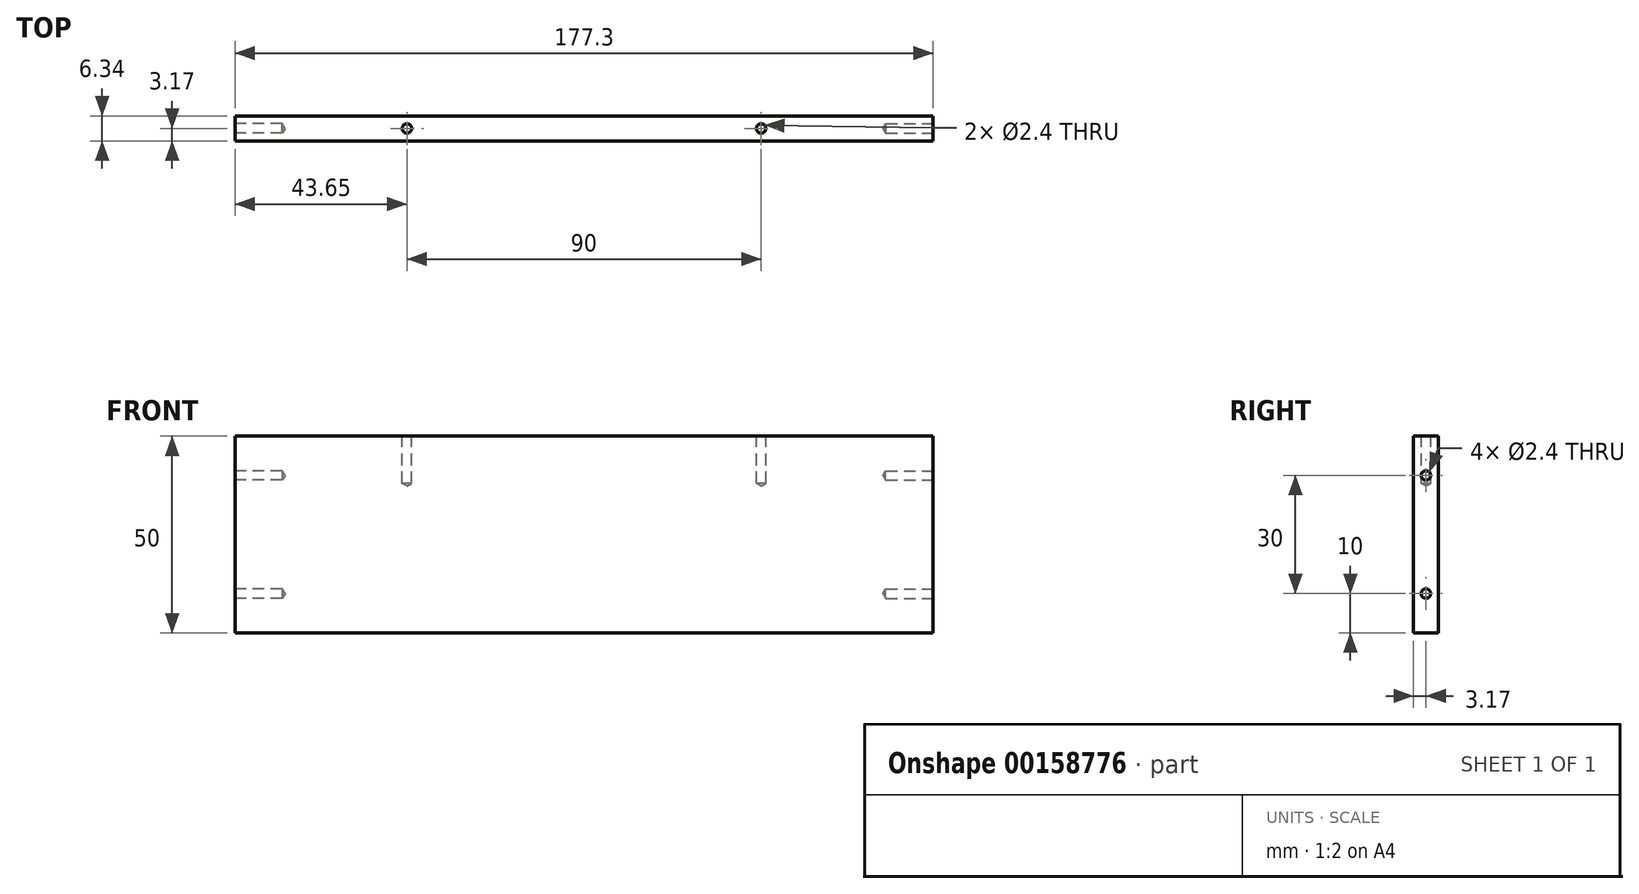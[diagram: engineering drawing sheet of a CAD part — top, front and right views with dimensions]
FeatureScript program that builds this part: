
annotation { "Feature Type Name" : "Feature", "Feature Type Description" : "" }
export const myFeature = defineFeature(function(context is Context, id is Id, definition is map)
    precondition{}
    {
        {
            var Q0;
            Q0=qCreatedBy(makeId("Front.planeOp"),FACE);
            var sketch = newSketch(context, id + "F0", { "sketchPlane" : qUnion([Q0])});
            skLineSegment(sketch, "E0.bottom", {"start": v(88.65, -25) * mm, "end": v(-88.65, -25) * mm});
            skLineSegment(sketch, "E0.top", {"start": v(88.65, 25) * mm, "end": v(-88.65, 25) * mm});
            skLineSegment(sketch, "E0.left", {"start": v(88.65, -25) * mm, "end": v(88.65, 25) * mm});
            skLineSegment(sketch, "E0.right", {"start": v(-88.65, -25) * mm, "end": v(-88.65, 25) * mm});
            skPoint(sketch, "E0.middle", {"position": v(0, 0) * mm});
            skSolve(sketch);
        }
        {
            var Q0;
            Q0=qSketchRegion(id+"F0",true);
            extrude(context, id + "F1", {"entities" : qUnion([Q0]), "endBound" : BoundingType.SYMMETRIC, "depth" : 6.35 * mm});
        }
        {
            var Q0;
            Q0=makeQuery(id+"F1.opExtrude","SWEPT_FACE",FACE,{"disambiguationData":[OSD([sQuery(id+"F0.wireOp",EDGE,"E0.top")])]});
            var sketch = newSketch(context, id + "F2", { "sketchPlane" : qUnion([Q0])});
            skCircle(sketch, "E1", {"center": v(-45, 0) * mm, "radius": 1.5 * mm});
            skCircle(sketch, "E2.MirrorC", {"center": v(45, 0) * mm, "radius": 1.5 * mm});
            skSolve(sketch);
        }
        {
            var Q0;
            Q0=sQuery(id+"F2.wireOp",VERTEX,"E1.center");
            var Q1;
            Q1=sQuery(id+"F2.wireOp",VERTEX,"E2.MirrorC.center");
            var Q2;
            Q2=makeQuery(id+"F1.opExtrude","SWEPT_BODY",BODY,{"disambiguationData":[OSD([sQuery(id+"F0.wireOp",EDGE,"E0.bottom"),sQuery(id+"F0.wireOp",EDGE,"E0.top"),sQuery(id+"F0.wireOp",EDGE,"E0.left"),sQuery(id+"F0.wireOp",EDGE,"E0.right")])]});
            hole(context, id + "F3", {"style" : HoleStyle.SIMPLE, "endStyle" : HoleEndStyle.BLIND, "standardTappedOrClearance" : lookupTablePath({ "standard" : "ISO", "engagement" : "75%", "pitch" : "0.6 mm", "size" : "M3", "type" : "Tapped" }), "standardBlindInLast" : lookupTablePath({ "standard" : "ISO", "engagement" : "75%", "pitch" : "0.6 mm", "size" : "M3", "type" : "Tapped" }), "holeDiameter" : 2.4 * mm, "holeDepth" : 12 * mm, "locations" : qUnion([Q0, Q1]), "scope" : qUnion([Q2])});
        }
        {
            var Q0;
            Q0=makeQuery(id+"F1.opExtrude","SWEPT_FACE",FACE,{"disambiguationData":[OSD([sQuery(id+"F0.wireOp",EDGE,"E0.left")])]});
            var sketch = newSketch(context, id + "F4", { "sketchPlane" : qUnion([Q0])});
            skCircle(sketch, "E3", {"center": v(0, -15) * mm, "radius": 1.5 * mm});
            skCircle(sketch, "E4.MirrorC", {"center": v(0, 15) * mm, "radius": 1.5 * mm});
            skSolve(sketch);
        }
        {
            var Q0;
            Q0=makeQuery(id+"F1.opExtrude","SWEPT_FACE",FACE,{"disambiguationData":[OSD([sQuery(id+"F0.wireOp",EDGE,"E0.right")])]});
            var sketch = newSketch(context, id + "F5", { "sketchPlane" : qUnion([Q0])});
            skCircle(sketch, "E5", {"center": v(0, -15) * mm, "radius": 1.5 * mm});
            skCircle(sketch, "E6.MirrorC", {"center": v(0, 15) * mm, "radius": 1.5 * mm});
            skSolve(sketch);
        }
        {
            var Q0;
            Q0=sQuery(id+"F5.wireOp",VERTEX,"E6.MirrorC.center");
            var Q1;
            Q1=sQuery(id+"F5.wireOp",VERTEX,"E5.center");
            var Q2;
            Q2=sQuery(id+"F4.wireOp",VERTEX,"E4.MirrorC.center");
            var Q3;
            Q3=sQuery(id+"F4.wireOp",VERTEX,"E3.center");
            var Q4;
            Q4=makeQuery(id+"F1.opExtrude","SWEPT_BODY",BODY,{"disambiguationData":[OSD([sQuery(id+"F0.wireOp",EDGE,"E0.bottom"),sQuery(id+"F0.wireOp",EDGE,"E0.top"),sQuery(id+"F0.wireOp",EDGE,"E0.left"),sQuery(id+"F0.wireOp",EDGE,"E0.right")])]});
            hole(context, id + "F6", {"style" : HoleStyle.SIMPLE, "endStyle" : HoleEndStyle.BLIND, "standardTappedOrClearance" : lookupTablePath({ "standard" : "ISO", "engagement" : "75%", "pitch" : "0.6 mm", "size" : "M3", "type" : "Tapped" }), "standardBlindInLast" : lookupTablePath({ "standard" : "ISO", "engagement" : "75%", "pitch" : "0.6 mm", "size" : "M3", "type" : "Tapped" }), "holeDiameter" : 2.4 * mm, "holeDepth" : 12 * mm, "locations" : qUnion([Q0, Q1, Q2, Q3]), "scope" : qUnion([Q4])});
        }
    });
